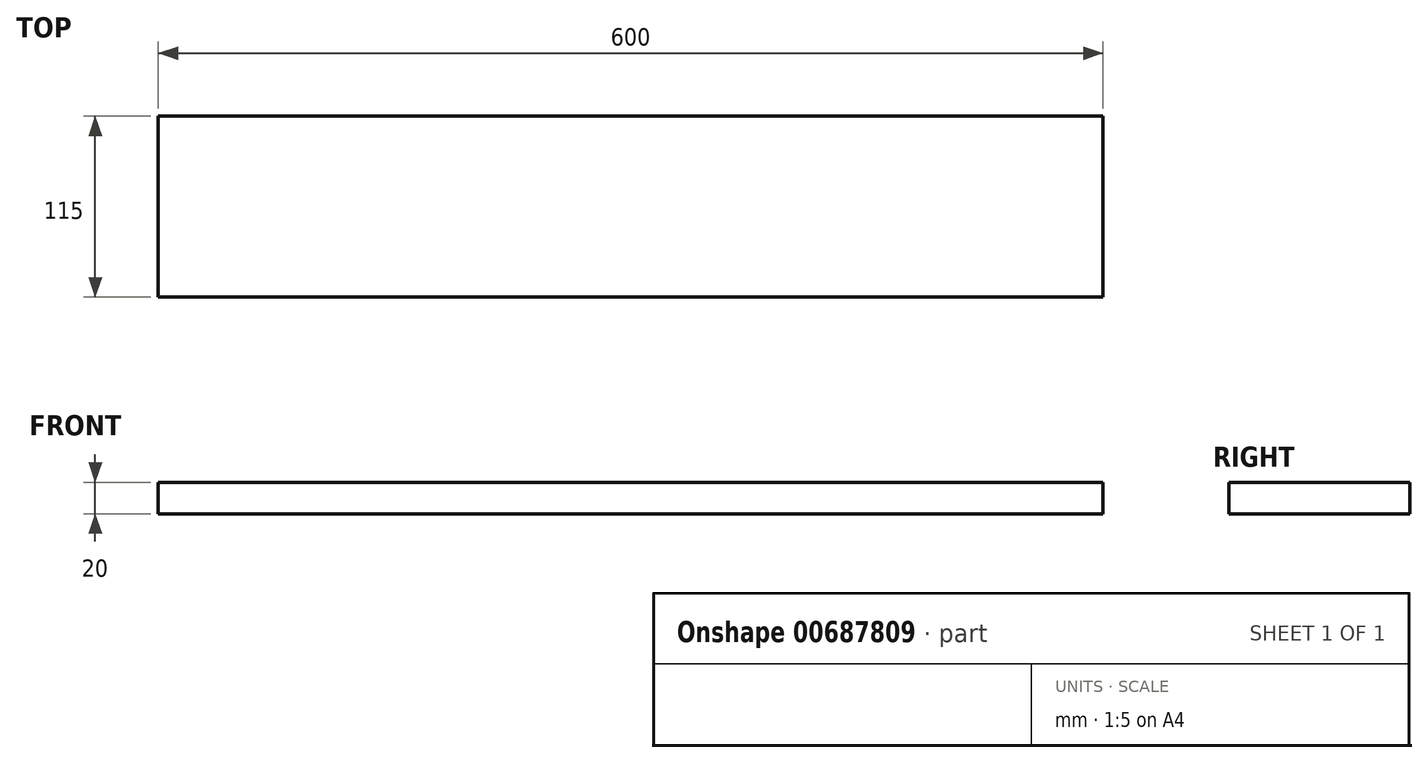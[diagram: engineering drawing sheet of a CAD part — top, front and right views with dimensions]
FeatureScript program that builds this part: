
annotation { "Feature Type Name" : "Feature", "Feature Type Description" : "" }
export const myFeature = defineFeature(function(context is Context, id is Id, definition is map)
    precondition{}
    {
        {
            var Q0;
            Q0=qCreatedBy(makeId("Top.planeOp"),FACE);
            var sketch = newSketch(context, id + "F0", { "sketchPlane" : qUnion([Q0])});
            skLineSegment(sketch, "E0.bottom", {"start": v(-558.77, 91.43) * mm, "end": v(41.23, 91.43) * mm});
            skLineSegment(sketch, "E0.top", {"start": v(-558.77, -23.57) * mm, "end": v(41.23, -23.57) * mm});
            skLineSegment(sketch, "E0.left", {"start": v(-558.77, 91.43) * mm, "end": v(-558.77, -23.57) * mm});
            skLineSegment(sketch, "E0.right", {"start": v(41.23, 91.43) * mm, "end": v(41.23, -23.57) * mm});
            skSolve(sketch);
        }
        {
            var Q0;
            Q0 = qSketchRegion(id + "F0", true);
            extrude(context, id + "F1", {"entities" : qUnion([Q0]), "depth" : 20 * mm, "offsetDistance" : 25 * mm});
        }
    });
